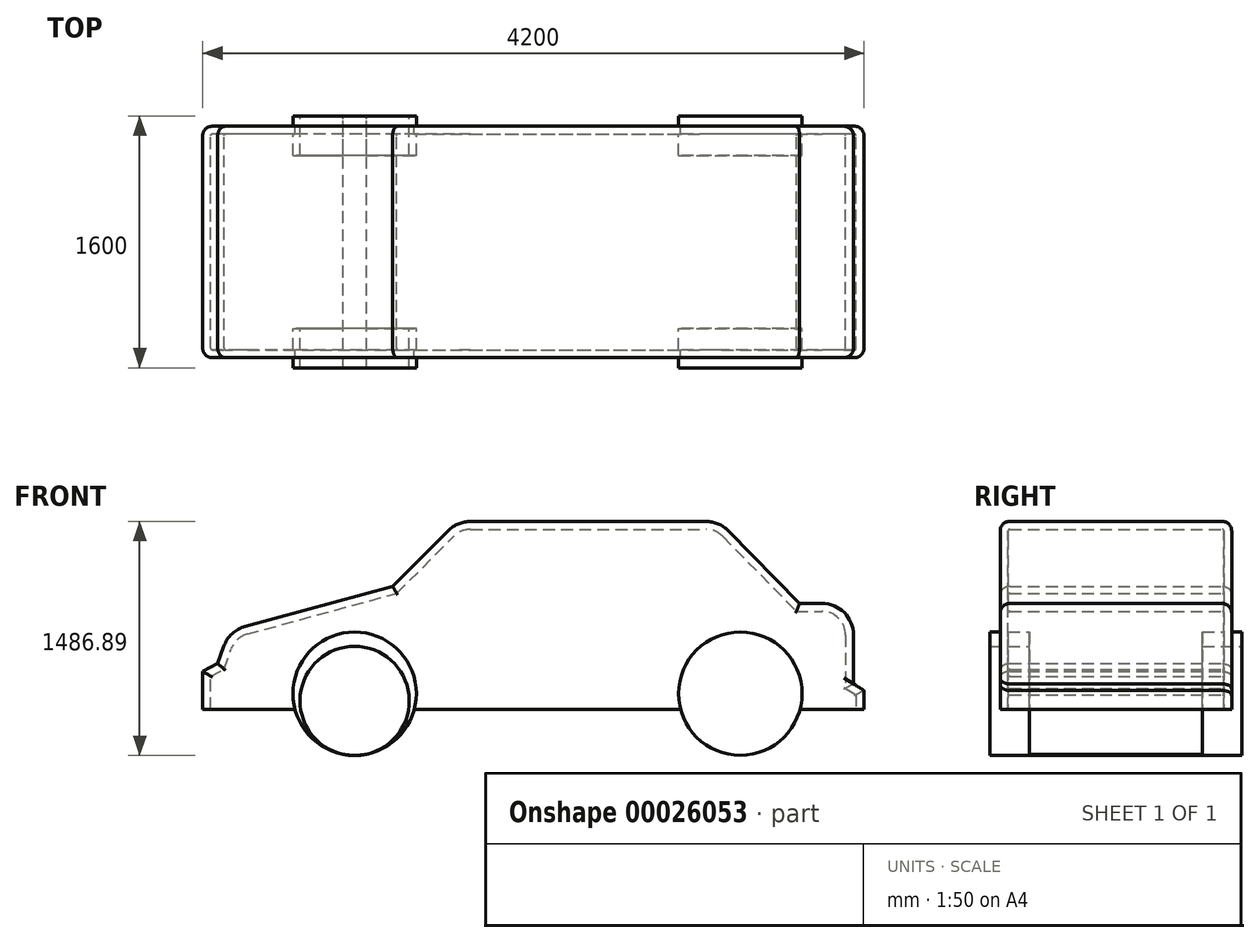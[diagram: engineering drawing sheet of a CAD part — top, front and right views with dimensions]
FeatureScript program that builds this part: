
annotation { "Feature Type Name" : "Feature", "Feature Type Description" : "" }
export const myFeature = defineFeature(function(context is Context, id is Id, definition is map)
    precondition{}
    {
        {
            var Q0;
            Q0=qCreatedBy(makeId("Front.planeOp"),FACE);
            var sketch = newSketch(context, id + "F0", { "sketchPlane" : qUnion([Q0])});
            skArc(sketch, "E0", {"start": v(378.92, -54.06) * mm, "mid": v(0, 382.75) * mm, "end": v(-378.92, -54.06) * mm});
            skArc(sketch, "E1", {"start": v(2828.92, -54.06) * mm, "mid": v(2450, 382.75) * mm, "end": v(2071.08, -54.06) * mm});
            skLineSegment(sketch, "E2", {"start": v(378.92, -54.06) * mm, "end": v(2071.08, -54.06) * mm});
            skLineSegment(sketch, "E3", {"start": v(-378.92, -54.06) * mm, "end": v(-964.38, -54.06) * mm});
            skLineSegment(sketch, "E4", {"start": v(-964.38, -54.06) * mm, "end": v(-964.38, 187.46) * mm});
            skLineSegment(sketch, "E5", {"start": v(-964.38, 187.46) * mm, "end": v(-869.25, 236.57) * mm});
            skLineSegment(sketch, "E6", {"start": v(-869.25, 236.57) * mm, "end": v(-795.6, 445.24) * mm});
            skLineSegment(sketch, "E7", {"start": v(-795.6, 445.24) * mm, "end": v(241.65, 727.57) * mm});
            skLineSegment(sketch, "E8", {"start": v(241.65, 727.57) * mm, "end": v(654.14, 1140.05) * mm});
            skLineSegment(sketch, "E9", {"start": v(654.14, 1140.05) * mm, "end": v(2315.57, 1140.05) * mm});
            skLineSegment(sketch, "E10", {"start": v(2315.57, 1140.05) * mm, "end": v(2826.52, 618.78) * mm});
            skLineSegment(sketch, "E11", {"start": v(2826.52, 618.78) * mm, "end": v(3168.53, 618.78) * mm});
            skLineSegment(sketch, "E12", {"start": v(3168.53, 618.78) * mm, "end": v(3168.53, 107.84) * mm});
            skLineSegment(sketch, "E13", {"start": v(3168.53, 107.84) * mm, "end": v(3235.62, 66.55) * mm});
            skLineSegment(sketch, "E14", {"start": v(3235.62, 66.55) * mm, "end": v(3235.62, -54.06) * mm});
            skLineSegment(sketch, "E15", {"start": v(3235.62, -54.06) * mm, "end": v(2828.92, -54.06) * mm});
            skCircle(sketch, "E16.0", {"center": v(0, 0) * mm, "radius": 346.84 * mm});
            skCircle(sketch, "E17.0", {"center": v(2450, 0) * mm, "radius": 332.75 * mm});
            skLineSegment(sketch, "E18", {"start": v(2121.67, -54.06) * mm, "end": v(2778.33, -54.06) * mm});
            skCircle(sketch, "E19", {"center": v(0, 46.02) * mm, "radius": 391.9 * mm});
            skCircle(sketch, "E20", {"center": v(2450, 46.02) * mm, "radius": 391.9 * mm});
            skSolve(sketch);
        }
        {
            var Q0;
            {var subQ1=sQuery(id+"F0.wireOp",EDGE,"E0");Q0=makeQuery(id+"F0.imprint","IMPRINT",FACE,{"disambiguationData":[TD([[makeQuery(id+"F0.imprint","IMPRINT",EDGE,{"derivedFrom":subQ1}),-1.0]])]});}
            var Q1;
            {var subQ2=sQuery(id+"F0.wireOp",EDGE,"E2");Q1=makeQuery(id+"F0.imprint","IMPRINT",FACE,{"disambiguationData":[TD([[makeQuery(id+"F0.imprint","IMPRINT",EDGE,{"derivedFrom":subQ2}),1.0]])]});}
            var Q2;
            {var subQ1=sQuery(id+"F0.wireOp",EDGE,"E1");Q2=makeQuery(id+"F0.imprint","IMPRINT",FACE,{"disambiguationData":[TD([[makeQuery(id+"F0.imprint","IMPRINT",EDGE,{"derivedFrom":subQ1}),-1.0]])]});}
            extrude(context, id + "F1", {"entities" : qUnion([Q0, Q1, Q2]), "endBound" : BoundingType.SYMMETRIC, "depth" : 1470 * mm});
        }
        {
            var Q0;
            Q0=makeQuery(id+"F1.opExtrude","CAP_EDGE",EDGE,{"disambiguationData":[OSD([sQuery(id+"F0.wireOp",EDGE,"E7")])],"isStart":false});
            var Q1;
            Q1=makeQuery(id+"F1.opExtrude","CAP_EDGE",EDGE,{"disambiguationData":[OSD([sQuery(id+"F0.wireOp",EDGE,"E6")])],"isStart":false});
            var Q2;
            Q2=makeQuery(id+"F1.opExtrude","CAP_EDGE",EDGE,{"disambiguationData":[OSD([sQuery(id+"F0.wireOp",EDGE,"E5")])],"isStart":false});
            var Q3;
            Q3=makeQuery(id+"F1.opExtrude","CAP_EDGE",EDGE,{"disambiguationData":[OSD([sQuery(id+"F0.wireOp",EDGE,"E4")])],"isStart":true});
            var Q4;
            Q4=makeQuery(id+"F1.opExtrude","CAP_EDGE",EDGE,{"disambiguationData":[OSD([sQuery(id+"F0.wireOp",EDGE,"E5")])],"isStart":true});
            var Q5;
            Q5=makeQuery(id+"F1.opExtrude","CAP_EDGE",EDGE,{"disambiguationData":[OSD([sQuery(id+"F0.wireOp",EDGE,"E6")])],"isStart":true});
            var Q6;
            Q6=makeQuery(id+"F1.opExtrude","CAP_EDGE",EDGE,{"disambiguationData":[OSD([sQuery(id+"F0.wireOp",EDGE,"E7")])],"isStart":true});
            var Q7;
            Q7=makeQuery(id+"F1.opExtrude","CAP_EDGE",EDGE,{"disambiguationData":[OSD([sQuery(id+"F0.wireOp",EDGE,"E4")])],"isStart":false});
            var Q8;
            Q8=makeQuery(id+"F1.opExtrude","CAP_EDGE",EDGE,{"disambiguationData":[OSD([sQuery(id+"F0.wireOp",EDGE,"E8")])],"isStart":false});
            var Q9;
            Q9=makeQuery(id+"F1.opExtrude","CAP_EDGE",EDGE,{"disambiguationData":[OSD([sQuery(id+"F0.wireOp",EDGE,"E8")])],"isStart":true});
            var Q10;
            Q10=makeQuery(id+"F1.opExtrude","CAP_EDGE",EDGE,{"disambiguationData":[OSD([sQuery(id+"F0.wireOp",EDGE,"E9")])],"isStart":false});
            var Q11;
            Q11=makeQuery(id+"F1.opExtrude","CAP_EDGE",EDGE,{"disambiguationData":[OSD([sQuery(id+"F0.wireOp",EDGE,"E9")])],"isStart":true});
            var Q12;
            Q12=makeQuery(id+"F1.opExtrude","CAP_EDGE",EDGE,{"disambiguationData":[OSD([sQuery(id+"F0.wireOp",EDGE,"E10")])],"isStart":true});
            var Q13;
            Q13=makeQuery(id+"F1.opExtrude","CAP_EDGE",EDGE,{"disambiguationData":[OSD([sQuery(id+"F0.wireOp",EDGE,"E10")])],"isStart":false});
            var Q14;
            Q14=makeQuery(id+"F1.opExtrude","CAP_EDGE",EDGE,{"disambiguationData":[OSD([sQuery(id+"F0.wireOp",EDGE,"E11")])],"isStart":false});
            var Q15;
            Q15=makeQuery(id+"F1.opExtrude","CAP_EDGE",EDGE,{"disambiguationData":[OSD([sQuery(id+"F0.wireOp",EDGE,"E11")])],"isStart":true});
            var Q16;
            Q16=makeQuery(id+"F1.opExtrude","CAP_EDGE",EDGE,{"disambiguationData":[OSD([sQuery(id+"F0.wireOp",EDGE,"E12")])],"isStart":true});
            var Q17;
            Q17=makeQuery(id+"F1.opExtrude","CAP_EDGE",EDGE,{"disambiguationData":[OSD([sQuery(id+"F0.wireOp",EDGE,"E12")])],"isStart":false});
            var Q18;
            Q18=makeQuery(id+"F1.opExtrude","CAP_EDGE",EDGE,{"disambiguationData":[OSD([sQuery(id+"F0.wireOp",EDGE,"E13")])],"isStart":true});
            var Q19;
            Q19=makeQuery(id+"F1.opExtrude","CAP_EDGE",EDGE,{"disambiguationData":[OSD([sQuery(id+"F0.wireOp",EDGE,"E14")])],"isStart":true});
            var Q20;
            Q20=makeQuery(id+"F1.opExtrude","CAP_EDGE",EDGE,{"disambiguationData":[OSD([sQuery(id+"F0.wireOp",EDGE,"E14")])],"isStart":false});
            fillet(context, id + "F2", {"entities" : qUnion([Q0, Q1, Q2, Q3, Q4, Q5, Q6, Q7, Q8, Q9, Q10, Q11, Q12, Q13, Q14, Q15, Q16, Q17, Q18, Q19, Q20]), "radius" : 60 * mm, "tangentPropagation" : true, "allowEdgeOverflow" : false});
        }
        {
            var Q0;
            Q0=makeQuery(id+"F1.opExtrude","SWEPT_EDGE",EDGE,{"disambiguationData":[OSD([sQuery(id+"F0.wireOp",EDGE,"E6"),sQuery(id+"F0.wireOp",EDGE,"E7")])]});
            var Q1;
            Q1=makeQuery(id+"F1.opExtrude","SWEPT_EDGE",EDGE,{"disambiguationData":[OSD([sQuery(id+"F0.wireOp",EDGE,"E8"),sQuery(id+"F0.wireOp",EDGE,"E9")])]});
            var Q2;
            Q2=makeQuery(id+"F1.opExtrude","SWEPT_EDGE",EDGE,{"disambiguationData":[OSD([sQuery(id+"F0.wireOp",EDGE,"E9"),sQuery(id+"F0.wireOp",EDGE,"E10")])]});
            var Q3;
            Q3=makeQuery(id+"F1.opExtrude","SWEPT_EDGE",EDGE,{"disambiguationData":[OSD([sQuery(id+"F0.wireOp",EDGE,"E11"),sQuery(id+"F0.wireOp",EDGE,"E12")])]});
            fillet(context, id + "F3", {"entities" : qUnion([Q0, Q1, Q2, Q3]), "radius" : 200 * mm, "tangentPropagation" : true, "allowEdgeOverflow" : false});
        }
        {
            var Q0;
            Q0=makeQuery(id+"F1.opExtrude","SWEPT_FACE",FACE,{"disambiguationData":[OSD([sQuery(id+"F0.wireOp",EDGE,"E3")])]});
            var Q1;
            Q1=makeQuery(id+"F1.opExtrude","SWEPT_FACE",FACE,{"disambiguationData":[OSD([sQuery(id+"F0.wireOp",EDGE,"E2")])]});
            var Q2;
            Q2=makeQuery(id+"F1.opExtrude","SWEPT_FACE",FACE,{"disambiguationData":[OSD([sQuery(id+"F0.wireOp",EDGE,"E0")])]});
            var Q3;
            Q3=makeQuery(id+"F1.opExtrude","SWEPT_FACE",FACE,{"disambiguationData":[OSD([sQuery(id+"F0.wireOp",EDGE,"E1")])]});
            var Q4;
            Q4=makeQuery(id+"F1.opExtrude","SWEPT_FACE",FACE,{"disambiguationData":[OSD([sQuery(id+"F0.wireOp",EDGE,"E15")])]});
            shell(context, id + "F4", {"entities" : qUnion([Q0, Q1, Q2, Q3, Q4]), "thickness" : 50 * mm});
        }
        {
            var Q0;
            {var subQ1=sQuery(id+"F0.wireOp",EDGE,"E0");Q0=makeQuery(id+"F0.imprint","IMPRINT",FACE,{"disambiguationData":[TD([[makeQuery(id+"F0.imprint","IMPRINT",EDGE,{"derivedFrom":subQ1}),-1.0]])]});}
            var Q1;
            {var subQ3=sQuery(id+"F0.wireOp",EDGE,"E0");Q1=makeQuery(id+"F0.imprint","IMPRINT",FACE,{"disambiguationData":[TD([[makeQuery(id+"F0.imprint","IMPRINT",EDGE,{"derivedFrom":subQ3}),1.0]])]});}
            var Q2;
            {var subQ0=sQuery(id+"F0.wireOp",EDGE,"E19");var subQ1=sQuery(id+"F0.wireOp",EDGE,"E16.0");var subQ3=makeQuery(id+"F0.imprint","INTERSECT",VERTEX,{"disambiguationData":[OD(0.0)],"derivedFrom":[subQ1,subQ0]});Q2=makeQuery(id+"F0.imprint","IMPRINT",FACE,{"disambiguationData":[TD([[makeQuery(id+"F0.imprint","IMPRINT",EDGE,{"disambiguationData":[TD([[subQ3,1.0]])],"derivedFrom":subQ1}),1.0]])]});}
            var Q3;
            {var subQ0=sQuery(id+"F0.wireOp",EDGE,"E18");Q3=makeQuery(id+"F0.imprint","IMPRINT",FACE,{"disambiguationData":[TD([[makeQuery(id+"F0.imprint","IMPRINT",EDGE,{"derivedFrom":subQ0}),-1.0]])]});}
            var Q4;
            {var subQ0=sQuery(id+"F0.wireOp",EDGE,"E18");Q4=makeQuery(id+"F0.imprint","IMPRINT",FACE,{"disambiguationData":[TD([[makeQuery(id+"F0.imprint","IMPRINT",EDGE,{"derivedFrom":subQ0}),1.0]])]});}
            var Q5;
            {var subQ1=sQuery(id+"F0.wireOp",EDGE,"E1");Q5=makeQuery(id+"F0.imprint","IMPRINT",FACE,{"disambiguationData":[TD([[makeQuery(id+"F0.imprint","IMPRINT",EDGE,{"derivedFrom":subQ1}),1.0]])]});}
            var Q6;
            {var subQ1=sQuery(id+"F0.wireOp",EDGE,"E1");Q6=makeQuery(id+"F0.imprint","IMPRINT",FACE,{"disambiguationData":[TD([[makeQuery(id+"F0.imprint","IMPRINT",EDGE,{"derivedFrom":subQ1}),-1.0]])]});}
            extrude(context, id + "F5", {"entities" : qUnion([Q0, Q1, Q2, Q3, Q4, Q5, Q6]), "operationType" : NewBodyOperationType.ADD, "endBound" : BoundingType.SYMMETRIC, "depth" : 1600 * mm});
        }
        {
            var Q0;
            Q0=qCreatedBy(makeId("Front.planeOp"),FACE);
            var sketch = newSketch(context, id + "F6", { "sketchPlane" : qUnion([Q0])});
            skCircle(sketch, "E21.0", {"center": v(0, 46.02) * mm, "radius": 391.9 * mm});
            skCircle(sketch, "E22.1", {"center": v(2450, 46.02) * mm, "radius": 391.9 * mm});
            skSolve(sketch);
        }
        {
            var Q0;
            Q0 = qSketchRegion(id + "F6", true);
            extrude(context, id + "F7", {"entities" : qUnion([Q0]), "operationType" : NewBodyOperationType.REMOVE, "endBound" : BoundingType.SYMMETRIC, "oppositeDirection" : true, "depth" : 1100 * mm});
        }
    });
